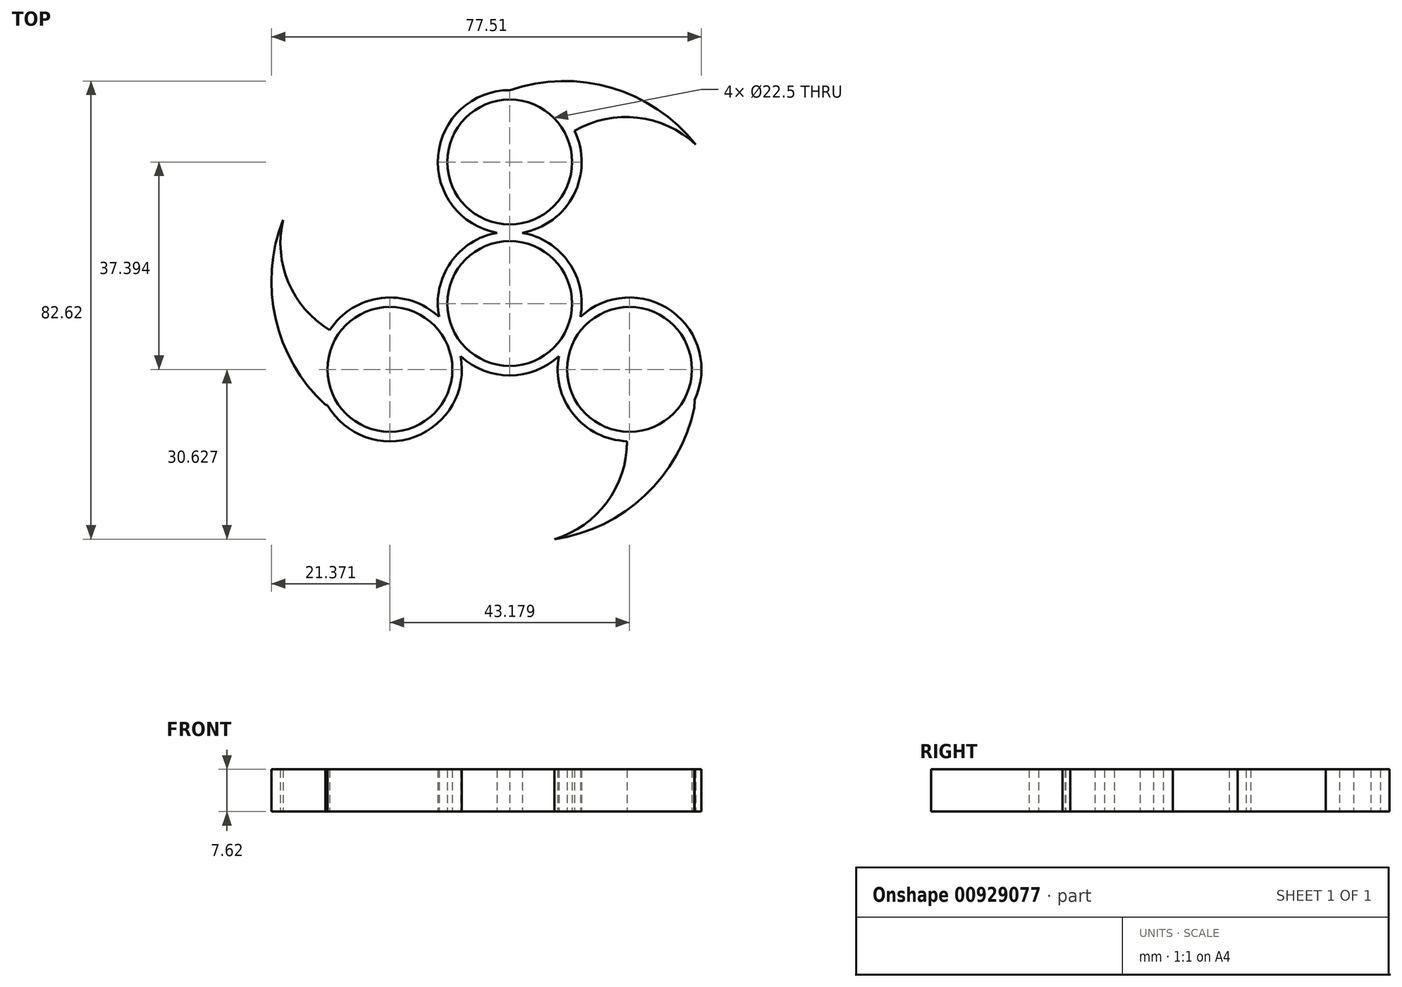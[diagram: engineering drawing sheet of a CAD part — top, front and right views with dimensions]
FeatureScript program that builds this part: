
annotation { "Feature Type Name" : "Feature", "Feature Type Description" : "" }
export const myFeature = defineFeature(function(context is Context, id is Id, definition is map)
    precondition{}
    {
        {
            var Q0;
            Q0=qCreatedBy(makeId("Top.planeOp"),FACE);
            var sketch = newSketch(context, id + "F0", { "sketchPlane" : qUnion([Q0])});
            skCircle(sketch, "E0", {"center": v(0, 0) * mm, "radius": 11.25 * mm});
            skCircle(sketch, "E1", {"center": v(0, 0) * mm, "radius": 12.96 * mm});
            skCircle(sketch, "E2", {"center": v(0, 25.52) * mm, "radius": 11.25 * mm});
            skCircle(sketch, "E3", {"center": v(0, 25.52) * mm, "radius": 12.96 * mm});
            skArc(sketch, "E4.1.0", {"start": v(-33.21, -18.25) * mm, "mid": v(-33.01, -18.3) * mm, "end": v(-32.81, -18.35) * mm});
            skCircle(sketch, "E4.1.2", {"center": v(-21.59, -11.87) * mm, "radius": 12.96 * mm});
            skCircle(sketch, "E4.1.3", {"center": v(-21.59, -11.87) * mm, "radius": 11.25 * mm});
            skArc(sketch, "E4.2.0", {"start": v(33.24, -18.81) * mm, "mid": v(33.03, -18.58) * mm, "end": v(32.81, -18.35) * mm});
            skCircle(sketch, "E4.2.2", {"center": v(21.59, -11.87) * mm, "radius": 12.96 * mm});
            skCircle(sketch, "E4.2.3", {"center": v(21.59, -11.87) * mm, "radius": 11.25 * mm});
            skPoint(sketch, "E4.center", {"position": v(0, 0.6) * mm});
            skPoint(sketch, "E5.end.orphan", {"position": v(0, 38.48) * mm});
            skArc(sketch, "E6", {"start": v(33.5, 28.67) * mm, "mid": v(18.31, 38.9) * mm, "end": v(0, 38.48) * mm});
            skArc(sketch, "E7", {"start": v(33.5, 28.67) * mm, "mid": v(23, 33.52) * mm, "end": v(11.68, 31.13) * mm});
            skArc(sketch, "E8.1.0", {"start": v(-40.84, 15.11) * mm, "mid": v(-42.1, -3.16) * mm, "end": v(-32.58, -18.81) * mm});
            skArc(sketch, "E8.1.1", {"start": v(-40.84, 15.11) * mm, "mid": v(-39.79, 3.6) * mm, "end": v(-32.06, -5.02) * mm});
            skArc(sketch, "E8.2.0", {"start": v(8.08, -42.5) * mm, "mid": v(24.53, -34.45) * mm, "end": v(33.33, -18.38) * mm});
            skArc(sketch, "E8.2.1", {"start": v(8.08, -42.5) * mm, "mid": v(17.53, -35.83) * mm, "end": v(21.12, -24.83) * mm});
            skPoint(sketch, "E8.center", {"position": v(0.25, 0.43) * mm});
            skPoint(sketch, "E9.orphan", {"position": v(-43.2, -11.5) * mm});
            skPoint(sketch, "E10.orphan", {"position": v(27.75, -23.28) * mm});
            skLineSegment(sketch, "E11", {"start": v(33.24, -18.81) * mm, "end": v(33.33, -17.37) * mm});
            skLineSegment(sketch, "E12", {"start": v(33.33, -17.37) * mm, "end": v(33.24, -18.81) * mm});
            skSolve(sketch);
        }
        {
            var Q0;
            Q0 = qSketchRegion(id + "F0", true);
            extrude(context, id + "F1", {"entities" : qUnion([Q0]), "depth" : 7.62 * mm, "offsetDistance" : 25.4 * mm});
        }
        {
            var Q0;
            {var subQ0=sQuery(id+"F0.wireOp",EDGE,"E4.2.0");Q0=makeQuery(id+"F0.imprint","IMPRINT",FACE,{"disambiguationData":[TD([[makeQuery(id+"F0.imprint","IMPRINT",EDGE,{"derivedFrom":subQ0}),1.0]])]});}
            var Q1;
            {var subQ0=sQuery(id+"F0.wireOp",EDGE,"E4.1.0");Q1=makeQuery(id+"F0.imprint","IMPRINT",FACE,{"disambiguationData":[TD([[makeQuery(id+"F0.imprint","IMPRINT",EDGE,{"derivedFrom":subQ0}),1.0]])]});}
            var Q2;
            {var subQ0=sQuery(id+"F0.wireOp",EDGE,"E6");Q2=makeQuery(id+"F0.imprint","IMPRINT",FACE,{"disambiguationData":[TD([[makeQuery(id+"F0.imprint","IMPRINT",EDGE,{"derivedFrom":subQ0}),1.0]])]});}
            var Q3;
            Q3=makeQuery(id+"F0.imprint","IMPRINT",FACE,{"disambiguationData":[TD([[makeQuery(id+"F0.imprint","IMPRINT",EDGE,{"derivedFrom":sQuery(id+"F0.wireOp",EDGE,"E2")}),-1.0]])]});
            var Q4;
            Q4=makeQuery(id+"F0.imprint","IMPRINT",FACE,{"disambiguationData":[TD([[makeQuery(id+"F0.imprint","IMPRINT",EDGE,{"derivedFrom":sQuery(id+"F0.wireOp",EDGE,"E0")}),-1.0]])]});
            var Q5;
            Q5=makeQuery(id+"F0.imprint","IMPRINT",FACE,{"disambiguationData":[TD([[makeQuery(id+"F0.imprint","IMPRINT",EDGE,{"derivedFrom":sQuery(id+"F0.wireOp",EDGE,"E4.2.3")}),-1.0]])]});
            var Q6;
            {var subQ0=sQuery(id+"F0.wireOp",EDGE,"E4.2.2");var subQ1=sQuery(id+"F0.wireOp",EDGE,"E1");var subQ2=makeQuery(id+"F0.imprint","INTERSECT",VERTEX,{"disambiguationData":[OD(0.0)],"derivedFrom":[subQ1,subQ0]});Q6=makeQuery(id+"F0.imprint","IMPRINT",FACE,{"disambiguationData":[TD([[makeQuery(id+"F0.imprint","IMPRINT",EDGE,{"disambiguationData":[TD([[subQ2,-1.0]])],"derivedFrom":subQ1}),1.0]])]});}
            var Q7;
            {var subQ0=sQuery(id+"F0.wireOp",EDGE,"E3");var subQ1=sQuery(id+"F0.wireOp",EDGE,"E1");var subQ2=makeQuery(id+"F0.imprint","INTERSECT",VERTEX,{"disambiguationData":[OD(0.0)],"derivedFrom":[subQ1,subQ0]});Q7=makeQuery(id+"F0.imprint","IMPRINT",FACE,{"disambiguationData":[TD([[makeQuery(id+"F0.imprint","IMPRINT",EDGE,{"disambiguationData":[TD([[subQ2,1.0]])],"derivedFrom":subQ1}),1.0]])]});}
            var Q8;
            {var subQ0=sQuery(id+"F0.wireOp",EDGE,"E4.1.2");var subQ1=sQuery(id+"F0.wireOp",EDGE,"E1");var subQ2=makeQuery(id+"F0.imprint","INTERSECT",VERTEX,{"disambiguationData":[OD(0.0)],"derivedFrom":[subQ1,subQ0]});Q8=makeQuery(id+"F0.imprint","IMPRINT",FACE,{"disambiguationData":[TD([[makeQuery(id+"F0.imprint","IMPRINT",EDGE,{"disambiguationData":[TD([[subQ2,-1.0]])],"derivedFrom":subQ1}),1.0]])]});}
            var Q9;
            Q9=makeQuery(id+"F0.imprint","IMPRINT",FACE,{"disambiguationData":[TD([[makeQuery(id+"F0.imprint","IMPRINT",EDGE,{"derivedFrom":sQuery(id+"F0.wireOp",EDGE,"E4.1.3")}),-1.0]])]});
            extrude(context, id + "F2", {"entities" : qUnion([Q0, Q1, Q2, Q3, Q4, Q5, Q6, Q7, Q8, Q9]), "operationType" : NewBodyOperationType.ADD, "depth" : 5.33 * mm, "offsetDistance" : 25.4 * mm});
        }
    });
